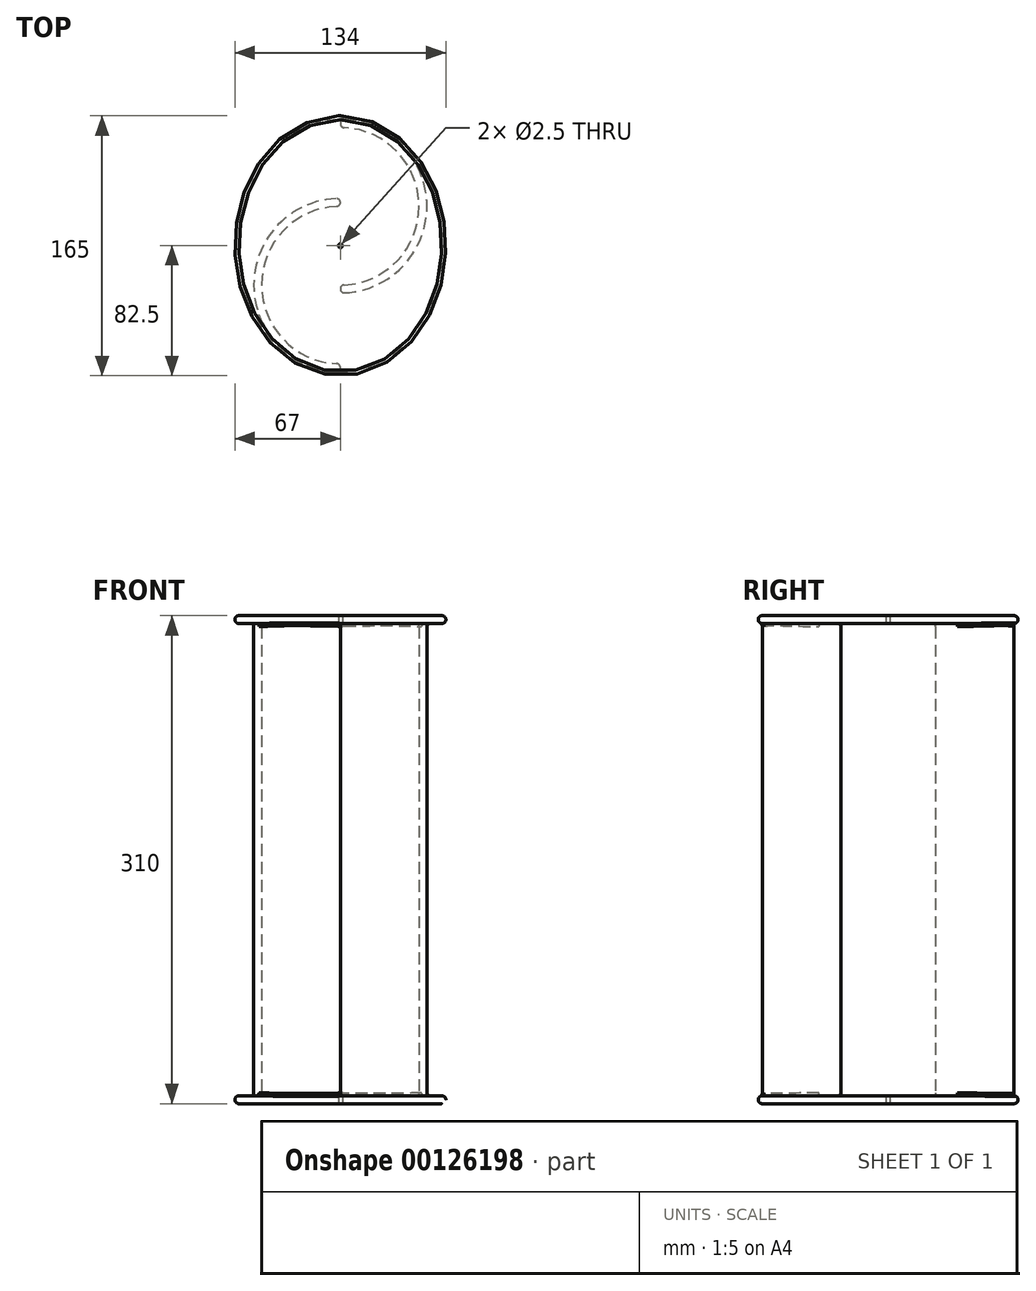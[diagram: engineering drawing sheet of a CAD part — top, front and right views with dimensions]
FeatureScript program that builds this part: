
annotation { "Feature Type Name" : "Feature", "Feature Type Description" : "" }
export const myFeature = defineFeature(function(context is Context, id is Id, definition is map)
    precondition{}
    {
        {
            var Q0;
            Q0=qCreatedBy(makeId("Top.planeOp"),FACE);
            var sketch = newSketch(context, id + "F0", { "sketchPlane" : qUnion([Q0])});
            skArc(sketch, "E0", {"start": v(0, -75) * mm, "mid": v(-50, -25) * mm, "end": v(0, 25) * mm});
            skArc(sketch, "E1", {"start": v(0, 75) * mm, "mid": v(50, 25) * mm, "end": v(0, -25) * mm});
            skArc(sketch, "E2.0", {"start": v(0, 80) * mm, "mid": v(55, 25) * mm, "end": v(0, -30) * mm});
            skArc(sketch, "E3.0", {"start": v(0, -80) * mm, "mid": v(-55, -25) * mm, "end": v(0, 30) * mm});
            skLineSegment(sketch, "E4", {"start": v(0, 75) * mm, "end": v(0, 80) * mm});
            skLineSegment(sketch, "E5", {"start": v(0, -30) * mm, "end": v(0, -25) * mm});
            skLineSegment(sketch, "E6", {"start": v(0, 25) * mm, "end": v(0, 30) * mm});
            skLineSegment(sketch, "E7", {"start": v(0, -80) * mm, "end": v(0, -75) * mm});
            skSolve(sketch);
        }
        {
            var Q0;
            Q0 = qSketchRegion(id + "F0", true);
            var Q1;
            Q1=makeQuery(id+"F0.imprint","IMPRINT",FACE,{"disambiguationData":[TD([[makeQuery(id+"F0.imprint","IMPRINT",EDGE,{"derivedFrom":sQuery(id+"F0.wireOp",EDGE,"E1")}),1.0]])]});
            extrude(context, id + "F1", {"entities" : qUnion([Q0, Q1]), "depth" : 300 * mm});
        }
        {
            var Q0;
            Q0=makeQuery(id+"F1.opExtrude","SWEPT_EDGE",EDGE,{"disambiguationData":[OSD([sQuery(id+"F0.wireOp",EDGE,"E0"),sQuery(id+"F0.wireOp",EDGE,"E7")])]});
            var Q1;
            Q1=makeQuery(id+"F1.opExtrude","SWEPT_EDGE",EDGE,{"disambiguationData":[OSD([sQuery(id+"F0.wireOp",EDGE,"E3.0"),sQuery(id+"F0.wireOp",EDGE,"E7")])]});
            var Q2;
            Q2=makeQuery(id+"F1.opExtrude","SWEPT_EDGE",EDGE,{"disambiguationData":[OSD([sQuery(id+"F0.wireOp",EDGE,"E3.0"),sQuery(id+"F0.wireOp",EDGE,"E6")])]});
            var Q3;
            Q3=makeQuery(id+"F1.opExtrude","SWEPT_EDGE",EDGE,{"disambiguationData":[OSD([sQuery(id+"F0.wireOp",EDGE,"E0"),sQuery(id+"F0.wireOp",EDGE,"E6")])]});
            var Q4;
            Q4=makeQuery(id+"F1.opExtrude","SWEPT_EDGE",EDGE,{"disambiguationData":[OSD([sQuery(id+"F0.wireOp",EDGE,"E1"),sQuery(id+"F0.wireOp",EDGE,"E5")])]});
            var Q5;
            Q5=makeQuery(id+"F1.opExtrude","SWEPT_EDGE",EDGE,{"disambiguationData":[OSD([sQuery(id+"F0.wireOp",EDGE,"E2.0"),sQuery(id+"F0.wireOp",EDGE,"E5")])]});
            var Q6;
            Q6=makeQuery(id+"F1.opExtrude","SWEPT_EDGE",EDGE,{"disambiguationData":[OSD([sQuery(id+"F0.wireOp",EDGE,"E1"),sQuery(id+"F0.wireOp",EDGE,"E4")])]});
            var Q7;
            Q7=makeQuery(id+"F1.opExtrude","SWEPT_EDGE",EDGE,{"disambiguationData":[OSD([sQuery(id+"F0.wireOp",EDGE,"E2.0"),sQuery(id+"F0.wireOp",EDGE,"E4")])]});
            fillet(context, id + "F2", {"entities" : qUnion([Q0, Q1, Q2, Q3, Q4, Q5, Q6, Q7]), "radius" : 2.5 * mm, "tangentPropagation" : true, "allowEdgeOverflow" : false});
        }
        {
            var Q0;
            Q0=qCreatedBy(makeId("Top.planeOp"),FACE);
            var sketch = newSketch(context, id + "F3", { "sketchPlane" : qUnion([Q0])});
            skEllipse(sketch, "E8", {"center": v(0, 0) * mm, "majorRadius": 82.5 * mm, "minorRadius": 67 * mm, "majorAxis": v(0, 1)});
            skSolve(sketch);
        }
        {
            var Q0;
            Q0 = qSketchRegion(id + "F3", true);
            extrude(context, id + "F4", {"entities" : qUnion([Q0]), "oppositeDirection" : true, "depth" : 5 * mm});
        }
        {
            var Q0;
            Q0=makeQuery(id+"F4.opExtrude","CAP_EDGE",EDGE,{"disambiguationData":[OSD([sQuery(id+"F3.wireOp",EDGE,"E8")])],"isStart":true});
            var Q1;
            Q1=makeQuery(id+"F4.opExtrude","CAP_EDGE",EDGE,{"disambiguationData":[OSD([sQuery(id+"F3.wireOp",EDGE,"E8")])],"isStart":false});
            fillet(context, id + "F5", {"entities" : qUnion([Q0, Q1]), "radius" : 2.5 * mm, "tangentPropagation" : true, "allowEdgeOverflow" : false});
        }
        {
            var Q0;
            Q0=makeQuery(id+"F4.opExtrude","SWEPT_BODY",BODY,{"disambiguationData":[OSD([sQuery(id+"F3.wireOp",EDGE,"E8")])]});
            transform(context, id + "F6", {"entities" : qUnion([Q0]), "transformType" : TransformType.TRANSLATION_3D, "dx" : 0 * mm, "dy" : 0 * mm, "dz" : 305 * mm, "makeCopy" : true});
        }
        {
            var Q0;
            Q0=makeQuery(id+"F1.opExtrude","SWEPT_BODY",BODY,{"disambiguationData":[OSD([sQuery(id+"F0.wireOp",EDGE,"E0"),sQuery(id+"F0.wireOp",EDGE,"E3.0"),sQuery(id+"F0.wireOp",EDGE,"E6"),sQuery(id+"F0.wireOp",EDGE,"E7")])]});
            var Q1;
            Q1=makeQuery(id+"F1.opExtrude","SWEPT_BODY",BODY,{"disambiguationData":[OSD([sQuery(id+"F0.wireOp",EDGE,"E1"),sQuery(id+"F0.wireOp",EDGE,"E2.0"),sQuery(id+"F0.wireOp",EDGE,"E4"),sQuery(id+"F0.wireOp",EDGE,"E5")])]});
            var Q2;
            Q2=makeQuery(id+"F4.opExtrude","SWEPT_BODY",BODY,{"disambiguationData":[OSD([sQuery(id+"F3.wireOp",EDGE,"E8")])]});
            var Q3;
            Q3=makeQuery(id+"F6.opPattern","COPY",BODY,{"derivedFrom":makeQuery(id+"F4.opExtrude","SWEPT_BODY",BODY,{"disambiguationData":[OSD([sQuery(id+"F3.wireOp",EDGE,"E8")])]}),"instanceName":"1"});
            booleanBodies(context, id + "F7", {"operationType" : BooleanOperationType.UNION, "tools" : qUnion([Q0, Q1, Q2, Q3])});
        }
        {
            var Q0;
            {var subQ0=sQuery(id+"F0.wireOp",EDGE,"E3.0");Q0=makeQuery(id+"F7.opBoolean","SPLIT",EDGE,{"disambiguationData":[TD([makeQuery(id+"F2.opFillet","BLEND_FACE",FACE,{"disambiguationData":[OSD([sQuery(id+"F0.wireOp",EDGE,"E0"),subQ0,sQuery(id+"F0.wireOp",EDGE,"E6")])]})])],"derivedFrom":makeQuery(id+"F1.opExtrude","CAP_EDGE",EDGE,{"disambiguationData":[OSD([subQ0])],"isStart":true})});}
            var Q1;
            Q1=makeQuery(id+"F1.opExtrude","CAP_EDGE",EDGE,{"disambiguationData":[OSD([sQuery(id+"F0.wireOp",EDGE,"E1")])],"isStart":true});
            var Q2;
            Q2=makeQuery(id+"F7.opBoolean","SPLIT",EDGE,{"derivedFrom":makeQuery(id+"F1.opExtrude","CAP_EDGE",EDGE,{"disambiguationData":[OSD([sQuery(id+"F0.wireOp",EDGE,"E3.0")])],"isStart":false})});
            var Q3;
            Q3=makeQuery(id+"F1.opExtrude","CAP_EDGE",EDGE,{"disambiguationData":[OSD([sQuery(id+"F0.wireOp",EDGE,"E1")])],"isStart":false});
            var Q4;
            Q4=makeQuery(id+"F7.opBoolean","SPLIT",EDGE,{"derivedFrom":makeQuery(id+"F1.opExtrude","CAP_EDGE",EDGE,{"disambiguationData":[OSD([sQuery(id+"F0.wireOp",EDGE,"E2.0")])],"isStart":false})});
            var Q5;
            {var subQ0=sQuery(id+"F0.wireOp",EDGE,"E2.0");Q5=makeQuery(id+"F7.opBoolean","SPLIT",EDGE,{"disambiguationData":[TD([makeQuery(id+"F2.opFillet","BLEND_FACE",FACE,{"disambiguationData":[OSD([subQ0,sQuery(id+"F0.wireOp",EDGE,"E5")])]})])],"derivedFrom":makeQuery(id+"F1.opExtrude","CAP_EDGE",EDGE,{"disambiguationData":[OSD([subQ0])],"isStart":true})});}
            var Q6;
            {var subQ0=sQuery(id+"F0.wireOp",EDGE,"E3.0");Q6=makeQuery(id+"F7.opBoolean","SPLIT",EDGE,{"disambiguationData":[TD([makeQuery(id+"F2.opFillet","BLEND_FACE",FACE,{"disambiguationData":[OSD([sQuery(id+"F0.wireOp",EDGE,"E0"),subQ0,sQuery(id+"F0.wireOp",EDGE,"E7")])]})])],"derivedFrom":makeQuery(id+"F1.opExtrude","CAP_EDGE",EDGE,{"disambiguationData":[OSD([subQ0])],"isStart":true})});}
            var Q7;
            Q7=makeQuery(id+"F1.opExtrude","CAP_EDGE",EDGE,{"disambiguationData":[OSD([sQuery(id+"F0.wireOp",EDGE,"E0")])],"isStart":false});
            fillet(context, id + "F8", {"entities" : qUnion([Q0, Q1, Q2, Q3, Q4, Q5, Q6, Q7]), "radius" : 2 * mm, "tangentPropagation" : true, "allowEdgeOverflow" : false});
        }
        {
            var Q0;
            Q0=qCreatedBy(makeId("Top.planeOp"),FACE);
            var sketch = newSketch(context, id + "F9", { "sketchPlane" : qUnion([Q0])});
            skCircle(sketch, "E9", {"center": v(0, 0) * mm, "radius": 1.25 * mm});
            skSolve(sketch);
        }
        {
            var Q0;
            Q0 = qSketchRegion(id + "F9", true);
            extrude(context, id + "F10", {"entities" : qUnion([Q0]), "operationType" : NewBodyOperationType.REMOVE, "endBound" : BoundingType.SYMMETRIC, "depth" : 800 * mm});
        }
    });
